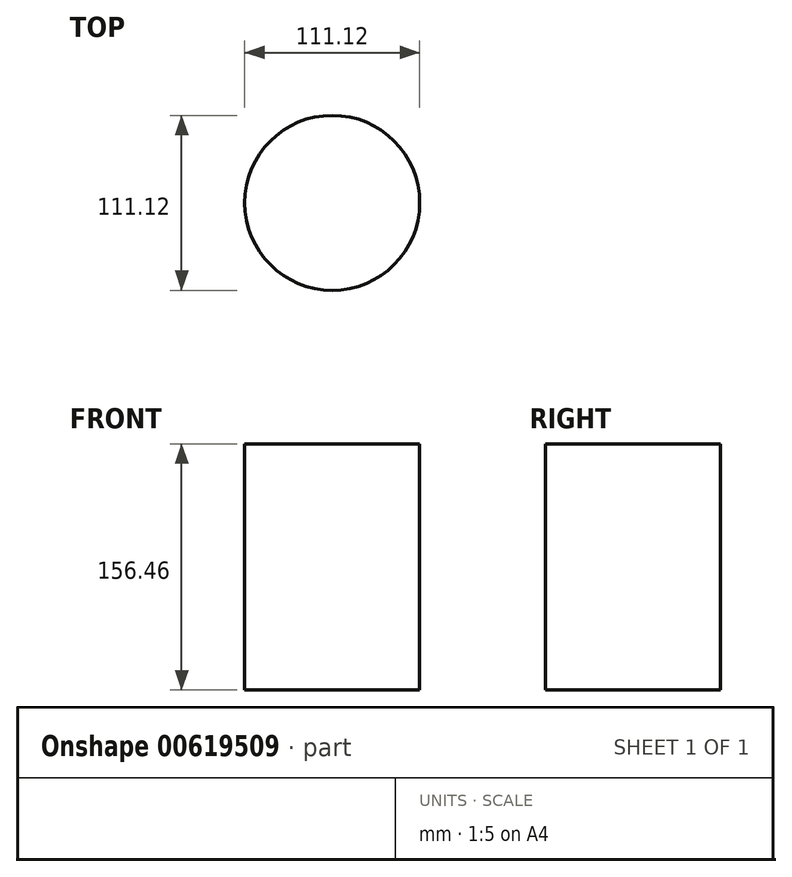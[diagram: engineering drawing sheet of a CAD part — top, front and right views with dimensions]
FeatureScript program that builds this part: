
annotation { "Feature Type Name" : "Feature", "Feature Type Description" : "" }
export const myFeature = defineFeature(function(context is Context, id is Id, definition is map)
    precondition{}
    {
        {
            var Q0;
            Q0=qCreatedBy(makeId("Top.planeOp"),FACE);
            var sketch = newSketch(context, id + "F0", { "sketchPlane" : qUnion([Q0])});
            skCircle(sketch, "E0", {"center": v(0, 0) * mm, "radius": 55.56 * mm});
            skSolve(sketch);
        }
        {
            var Q0;
            Q0=makeQuery(id+"F0.imprint","IMPRINT",FACE,{"disambiguationData":[TD([[makeQuery(id+"F0.imprint","IMPRINT",EDGE,{"derivedFrom":sQuery(id+"F0.wireOp",EDGE,"E0")}),1.0]])]});
            extrude(context, id + "F1", {"entities" : qUnion([Q0]), "depth" : 156.46 * mm, "offsetDistance" : 25.4 * mm});
        }
    });
